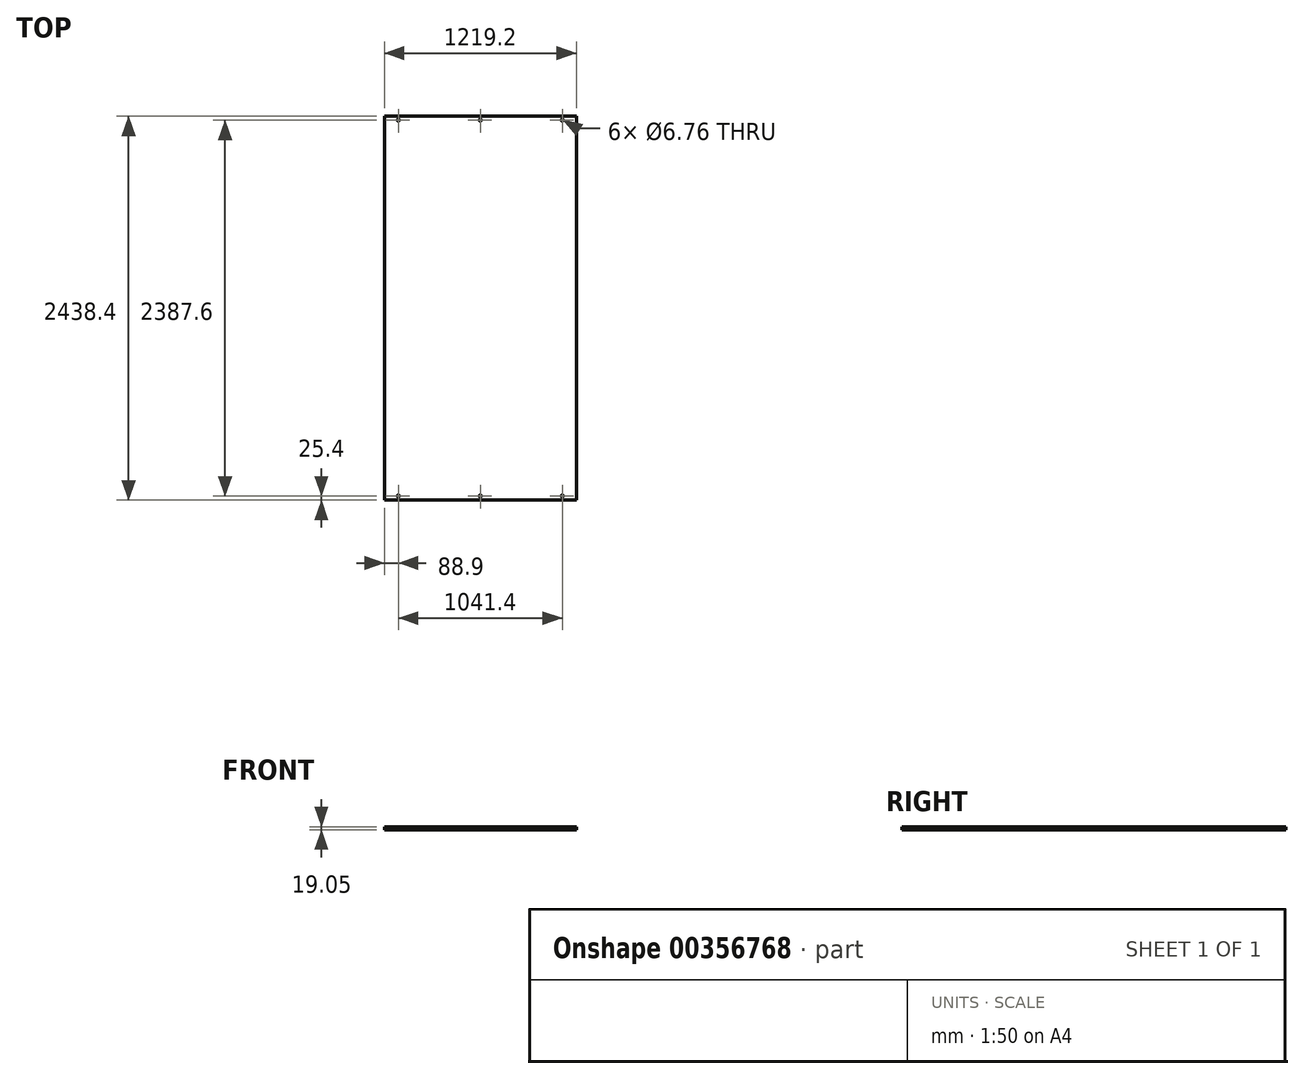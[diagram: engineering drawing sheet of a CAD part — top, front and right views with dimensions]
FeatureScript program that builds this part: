
annotation { "Feature Type Name" : "Feature", "Feature Type Description" : "" }
export const myFeature = defineFeature(function(context is Context, id is Id, definition is map)
    precondition{}
    {
        {
            var Q0;
            Q0=qCreatedBy(makeId("Top.planeOp"),FACE);
            var sketch = newSketch(context, id + "F0", { "sketchPlane" : qUnion([Q0])});
            skLineSegment(sketch, "E0.bottom", {"start": v(609.6, -1219.2) * mm, "end": v(-609.6, -1219.2) * mm});
            skLineSegment(sketch, "E0.top", {"start": v(609.6, 1219.2) * mm, "end": v(-609.6, 1219.2) * mm});
            skLineSegment(sketch, "E0.left", {"start": v(609.6, -1219.2) * mm, "end": v(609.6, 1219.2) * mm});
            skLineSegment(sketch, "E0.right", {"start": v(-609.6, -1219.2) * mm, "end": v(-609.6, 1219.2) * mm});
            skPoint(sketch, "E0.middle", {"position": v(0, 0) * mm});
            skSolve(sketch);
        }
        {
            var Q0;
            Q0=makeQuery(id+"F0.imprint","IMPRINT",FACE,{"disambiguationData":[TD([[makeQuery(id+"F0.imprint","IMPRINT",EDGE,{"derivedFrom":sQuery(id+"F0.wireOp",EDGE,"E0.bottom")}),-1.0]])]});
            extrude(context, id + "F1", {"entities" : qUnion([Q0]), "depth" : 19.05 * mm});
        }
        {
            var Q0;
            Q0=makeQuery(id+"F1.opExtrude","CAP_FACE",FACE,{"disambiguationData":[OSD([sQuery(id+"F0.wireOp",EDGE,"E0.bottom"),sQuery(id+"F0.wireOp",EDGE,"E0.top"),sQuery(id+"F0.wireOp",EDGE,"E0.left"),sQuery(id+"F0.wireOp",EDGE,"E0.right")])],"isStart":false});
            var sketch = newSketch(context, id + "F2", { "sketchPlane" : qUnion([Q0])});
            skPoint(sketch, "E1", {"position": v(-520.7, -1193.8) * mm});
            skLineSegment(sketch, "E2", {"start": v(-609.6, 0) * mm, "end": v(609.6, 0) * mm, "construction": true});
            skLineSegment(sketch, "E3", {"start": v(0, 1219.2) * mm, "end": v(0, -1219.2) * mm, "construction": true});
            skPoint(sketch, "E4.MirrorP", {"position": v(520.7, -1193.8) * mm});
            skPoint(sketch, "E5.MirrorP", {"position": v(520.7, 1193.8) * mm});
            skPoint(sketch, "E6.MirrorP", {"position": v(-520.7, 1193.8) * mm});
            skPoint(sketch, "E7", {"position": v(-520.7, 0) * mm});
            skPoint(sketch, "E8", {"position": v(520.7, 0) * mm});
            skPoint(sketch, "E9", {"position": v(0, 1193.8) * mm});
            skPoint(sketch, "E10", {"position": v(0, -1193.8) * mm});
            skPoint(sketch, "E11", {"position": v(0, 0) * mm});
            skPoint(sketch, "E12", {"position": v(-520.7, -596.9) * mm});
            skPoint(sketch, "E13", {"position": v(520.7, -596.9) * mm});
            skPoint(sketch, "E14", {"position": v(0, -596.9) * mm});
            skPoint(sketch, "E15.MirrorP", {"position": v(520.7, 596.9) * mm});
            skPoint(sketch, "E16.MirrorP", {"position": v(0, 596.9) * mm});
            skPoint(sketch, "E17.MirrorP", {"position": v(-520.7, 596.9) * mm});
            skSolve(sketch);
        }
        {
            var Q0;
            Q0=sQuery(id+"F2.wireOp",VERTEX,"E1");
            var Q1;
            Q1=sQuery(id+"F2.wireOp",VERTEX,"E10");
            var Q2;
            Q2=sQuery(id+"F2.wireOp",VERTEX,"E4.MirrorP");
            var Q3;
            Q3=sQuery(id+"F2.wireOp",VERTEX,"E5.MirrorP");
            var Q4;
            Q4=sQuery(id+"F2.wireOp",VERTEX,"E9");
            var Q5;
            Q5=sQuery(id+"F2.wireOp",VERTEX,"E6.MirrorP");
            var Q6;
            Q6=makeQuery(id+"F1.opExtrude","SWEPT_BODY",BODY,{"disambiguationData":[OSD([sQuery(id+"F0.wireOp",EDGE,"E0.bottom"),sQuery(id+"F0.wireOp",EDGE,"E0.top"),sQuery(id+"F0.wireOp",EDGE,"E0.left"),sQuery(id+"F0.wireOp",EDGE,"E0.right")])]});
            hole(context, id + "F3", {"style" : HoleStyle.C_SINK, "endStyle" : HoleEndStyle.BLIND, "standardTappedOrClearance" : lookupTablePath({ "standard" : "ANSI", "fit" : "Normal (ASME)", "size" : "1/4", "type" : "Clearance" }), "standardBlindInLast" : lookupTablePath({ "fit" : "Free", "standard" : "ANSI", "size" : "1/4", "type" : "Clearance" }), "holeDiameter" : 6.76 * mm, "cSinkDiameter" : 13.5 * mm, "cSinkAngle" : 82 * degree, "holeDepth" : 25.4 * mm, "isTappedThrough" : true, "tappedDepth" : 12.7 * mm, "tapClearance" : 3, "locations" : qUnion([Q0, Q1, Q2, Q3, Q4, Q5]), "scope" : qUnion([Q6])});
        }
    });
